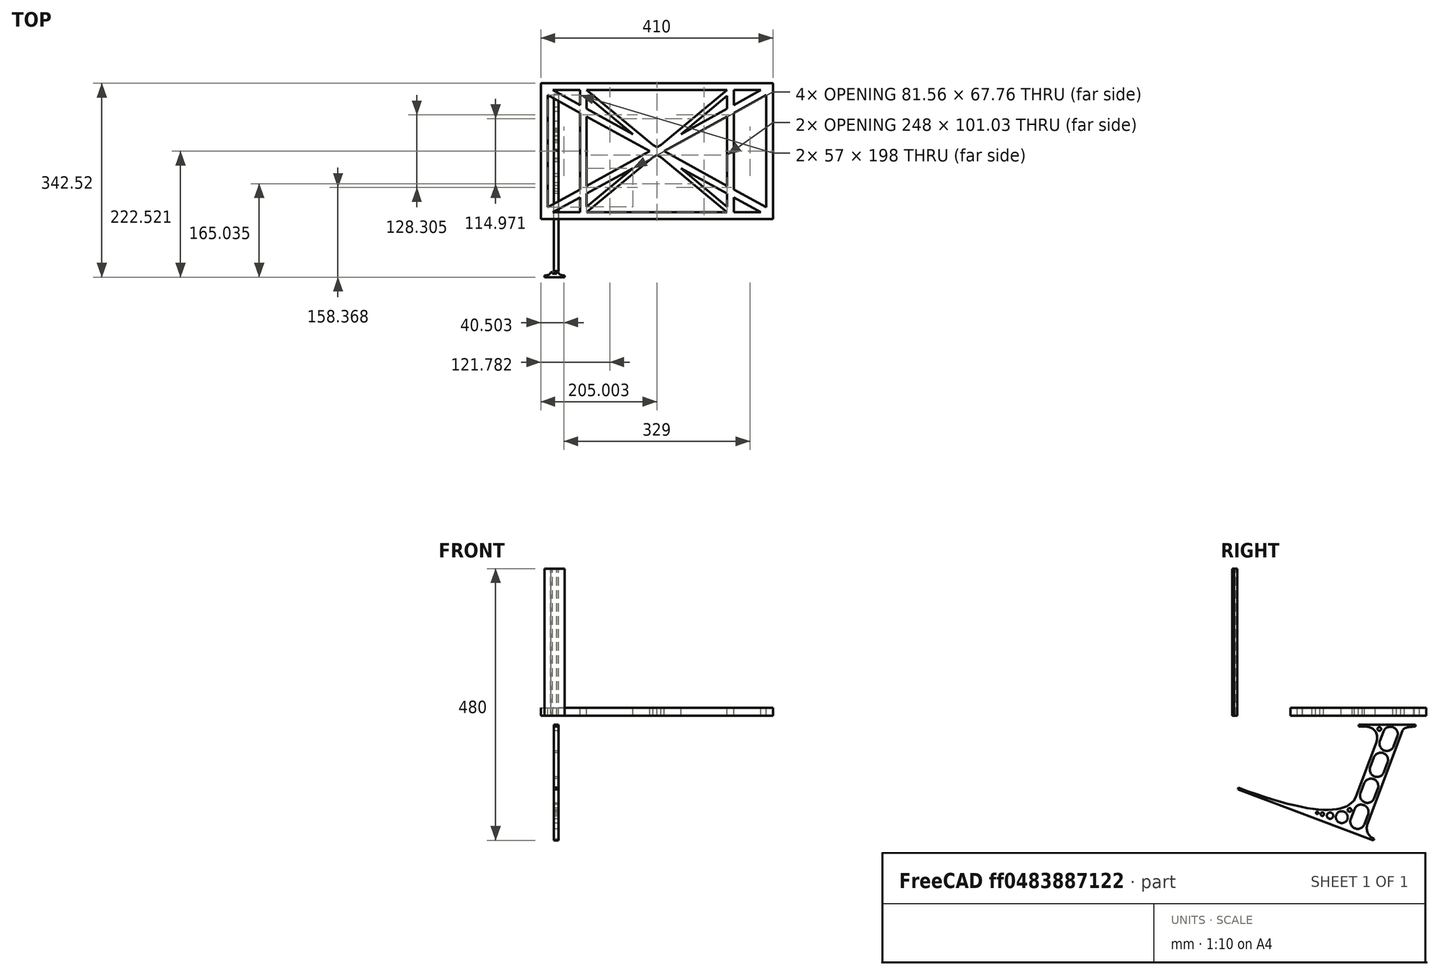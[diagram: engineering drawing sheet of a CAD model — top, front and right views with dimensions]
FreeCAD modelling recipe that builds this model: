
FCSTD DOCUMENT  (FreeCAD 0.19R0.19.2)
Label: laptopStand048
License: All rights reserved
LicenseURL: http://en.wikipedia.org/wiki/All_rights_reserved
objects: Sketcher::SketchObject×3, Part::Extrusion×3
note: 6 computed .brp shape members not serialized (recipe doc carries the construction recipe); baked Part::Feature solids carry a one-line shape summary decoded from their .brp

FEATURE [Sketcher::SketchObject] Sketch
  FullyConstrained = false
  sketch-geometry (70):
    g0: LineSegment StartX=-22.9272 StartY=136.221 StartZ=0 EndX=387.073 EndY=136.221 EndZ=0
    g1: LineSegment StartX=-22.9272 StartY=-103.779 StartZ=0 EndX=387.073 EndY=-103.779 EndZ=0
    g2: LineSegment StartX=375.073 StartY=115.221 StartZ=0 EndX=318.073 EndY=83.9235 EndZ=0
    g3: LineSegment StartX=-10.9272 StartY=-82.7794 StartZ=0 EndX=46.0728 EndY=-51.4823 EndZ=0
    g4: LineSegment StartX=-1.92719 StartY=124.221 StartZ=0 EndX=46.0728 EndY=97.8651 EndZ=0
    g5: LineSegment StartX=366.073 StartY=-91.7794 StartZ=0 EndX=318.073 EndY=-65.424 EndZ=0
    g6: LineSegment StartX=-10.9272 StartY=115.221 StartZ=0 EndX=-10.9272 EndY=-82.7794 EndZ=0
    g7: LineSegment StartX=375.073 StartY=-82.7794 StartZ=0 EndX=375.073 EndY=115.221 EndZ=0
    g8: LineSegment StartX=-1.92719 StartY=-91.7794 StartZ=0 EndX=46.0728 EndY=-91.7794 EndZ=0
    g9: LineSegment StartX=318.073 StartY=124.221 StartZ=0 EndX=366.073 EndY=124.221 EndZ=0
    g10: LineSegment StartX=306.073 StartY=-81.8102 StartZ=0 EndX=224.513 EndY=-14.0532 EndZ=0
    g11: LineSegment StartX=58.0728 StartY=114.251 StartZ=0 EndX=139.632 EndY=46.4944 EndZ=0
    g12: LineSegment StartX=306.073 StartY=124.221 StartZ=0 EndX=189.124 EndY=27.0628 EndZ=0
    g13: LineSegment StartX=58.0728 StartY=-91.7794 StartZ=0 EndX=175.022 EndY=5.37834 EndZ=0
    g14: LineSegment StartX=46.0728 StartY=124.221 StartZ=0 EndX=46.0728 EndY=97.8651 EndZ=0
    g15: LineSegment StartX=58.0728 StartY=-81.8102 StartZ=0 EndX=58.0728 EndY=-58.8351 EndZ=0
    g16: LineSegment StartX=318.073 StartY=124.221 StartZ=0 EndX=318.073 EndY=97.8651 EndZ=0
    g17: LineSegment StartX=306.073 StartY=114.251 StartZ=0 EndX=306.073 EndY=91.2763 EndZ=0
    g18: LineSegment StartX=224.513 StartY=46.4944 StartZ=0 EndX=306.073 EndY=114.251 EndZ=0
    g19: LineSegment StartX=175.022 StartY=27.0628 StartZ=0 EndX=58.0728 EndY=124.221 EndZ=0
    g20: LineSegment StartX=169.377 StartY=16.2206 StartZ=0 EndX=58.0728 EndY=77.3346 EndZ=0
    g21: LineSegment StartX=139.632 StartY=-14.0532 StartZ=0 EndX=58.0728 EndY=-81.8102 EndZ=0
    g22: LineSegment StartX=194.768 StartY=16.2206 StartZ=0 EndX=306.073 EndY=-44.8935 EndZ=0
    g23: LineSegment StartX=224.513 StartY=46.4944 StartZ=0 EndX=306.073 EndY=91.2763 EndZ=0
    g24: LineSegment StartX=175.022 StartY=27.0628 StartZ=0 EndX=179.022 EndY=24.8665 EndZ=0
    g25: LineSegment StartX=139.632 StartY=-14.0532 StartZ=0 EndX=58.0728 EndY=-58.8351 EndZ=0
    g26: LineSegment StartX=189.124 StartY=5.37834 StartZ=0 EndX=185.124 EndY=7.57463 EndZ=0
    g27: LineSegment StartX=189.124 StartY=5.37834 StartZ=0 EndX=306.073 EndY=-91.7794 EndZ=0
    g28: LineSegment StartX=306.073 StartY=77.3346 StartZ=0 EndX=306.073 EndY=-44.8935 EndZ=0
    g29: LineSegment StartX=318.073 StartY=83.9235 StartZ=0 EndX=318.073 EndY=-51.4823 EndZ=0
    g30: LineSegment StartX=318.073 StartY=97.8651 StartZ=0 EndX=366.073 EndY=124.221 EndZ=0
    g31: LineSegment StartX=306.073 StartY=77.3346 StartZ=0 EndX=194.768 EndY=16.2206 EndZ=0
    g32: LineSegment StartX=306.073 StartY=-58.8351 StartZ=0 EndX=224.513 EndY=-14.0532 EndZ=0
    g33: LineSegment StartX=306.073 StartY=-58.8351 StartZ=0 EndX=306.073 EndY=-81.8102 EndZ=0
    g34: LineSegment StartX=318.073 StartY=-51.4823 StartZ=0 EndX=375.073 EndY=-82.7794 EndZ=0
    g35: LineSegment StartX=318.073 StartY=-65.424 StartZ=0 EndX=318.073 EndY=-91.7794 EndZ=0
    g36: LineSegment StartX=318.073 StartY=-91.7794 StartZ=0 EndX=366.073 EndY=-91.7794 EndZ=0
    g37: LineSegment StartX=58.0728 StartY=-44.8935 StartZ=0 EndX=58.0728 EndY=77.3346 EndZ=0
    g38: LineSegment StartX=46.0728 StartY=-65.424 StartZ=0 EndX=-1.92719 EndY=-91.7794 EndZ=0
    g39: LineSegment StartX=46.0728 StartY=-65.424 StartZ=0 EndX=46.0728 EndY=-91.7794 EndZ=0
    g40: LineSegment StartX=58.0728 StartY=-44.8935 StartZ=0 EndX=169.377 EndY=16.2206 EndZ=0
    g41: LineSegment StartX=58.0728 StartY=91.2763 StartZ=0 EndX=58.0728 EndY=114.251 EndZ=0
    g42: LineSegment StartX=46.0728 StartY=83.9235 StartZ=0 EndX=46.0728 EndY=-51.4823 EndZ=0
    g43: LineSegment StartX=46.0728 StartY=124.221 StartZ=0 EndX=-1.92719 EndY=124.221 EndZ=0
    g44: LineSegment StartX=58.0728 StartY=91.2763 StartZ=0 EndX=139.632 EndY=46.4944 EndZ=0
    g45: LineSegment StartX=46.0728 StartY=83.9235 StartZ=0 EndX=-10.9272 EndY=115.221 EndZ=0
    g46: LineSegment StartX=-22.9272 StartY=136.221 StartZ=0 EndX=-42.9272 EndY=136.221 EndZ=0
    g47: LineSegment StartX=387.073 StartY=136.221 StartZ=0 EndX=407.073 EndY=136.221 EndZ=0
    g48: LineSegment StartX=-42.9272 StartY=136.221 StartZ=0 EndX=-42.9272 EndY=-103.779 EndZ=0
    g49: LineSegment StartX=-22.9272 StartY=-103.779 StartZ=0 EndX=-42.9272 EndY=-103.779 EndZ=0
    g50: LineSegment StartX=407.073 StartY=136.221 StartZ=0 EndX=407.073 EndY=-103.779 EndZ=0
    g51: LineSegment StartX=387.073 StartY=-103.779 StartZ=0 EndX=407.073 EndY=-103.779 EndZ=0
    g52: LineSegment StartX=179.022 StartY=27.0628 StartZ=0 EndX=179.022 EndY=124.221 EndZ=0
    g53: LineSegment StartX=185.124 StartY=27.0628 StartZ=0 EndX=185.124 EndY=124.221 EndZ=0
    g54: LineSegment StartX=179.022 StartY=27.0628 StartZ=0 EndX=179.022 EndY=24.8665 EndZ=0
    g55: LineSegment StartX=185.124 StartY=27.0628 StartZ=0 EndX=185.124 EndY=24.8665 EndZ=0
    g56: LineSegment StartX=185.124 StartY=7.57463 StartZ=0 EndX=185.124 EndY=-91.7794 EndZ=0
    g57: LineSegment StartX=179.022 StartY=7.57463 StartZ=0 EndX=179.022 EndY=-91.7794 EndZ=0
    g58: LineSegment StartX=189.124 StartY=27.0628 StartZ=0 EndX=185.124 EndY=24.8665 EndZ=0
    g59: LineSegment StartX=175.022 StartY=5.37834 StartZ=0 EndX=179.022 EndY=7.57463 EndZ=0
    g60: ArcOfCircle CenterX=-26.9272 CenterY=22.1087 CenterZ=0 NormalX=0 NormalY=0 NormalZ=1 AngleXU=0 Radius=8 StartAngle=1e-16 EndAngle=3.14159
    g61: ArcOfCircle CenterX=-26.9272 CenterY=-83.7794 CenterZ=0 NormalX=0 NormalY=0 NormalZ=1 AngleXU=0 Radius=8 StartAngle=3.14159 EndAngle=6.28319
    g62: LineSegment StartX=-34.9272 StartY=22.1087 StartZ=0 EndX=-34.9272 EndY=-83.7794 EndZ=0
    g63: LineSegment StartX=-18.9272 StartY=22.1087 StartZ=0 EndX=-18.9272 EndY=-83.7794 EndZ=0
    g64: LineSegment StartX=407.073 StartY=-91.7794 StartZ=0 EndX=391.073 EndY=-91.7794 EndZ=0
    g65: LineSegment StartX=391.073 StartY=-91.7794 StartZ=0 EndX=391.073 EndY=-83.7794 EndZ=0
    g66: LineSegment StartX=185.124 StartY=-91.7794 StartZ=0 EndX=306.073 EndY=-91.7794 EndZ=0
    g67: LineSegment StartX=179.022 StartY=-91.7794 StartZ=0 EndX=58.0728 EndY=-91.7794 EndZ=0
    g68: LineSegment StartX=306.073 StartY=124.221 StartZ=0 EndX=185.124 EndY=124.221 EndZ=0
    g69: LineSegment StartX=179.022 StartY=124.221 StartZ=0 EndX=58.0728 EndY=124.221 EndZ=0
  constraints (143):
    c: Horizontal(g0)
    c: Distance(g0) = 410
    c: Horizontal(g1)
    c: Block(g0)
    c: Horizontal(g8)
    c: Horizontal(g9)
    c: Tangent(g5,g20)
    c: PointOnObject(g20,g3)
    c: PointOnObject(g22,g2)
    c: Coincident(g44,g11)
    c: Coincident(g24,g19)
    c: Coincident(g18,g23)
    c: Coincident(g25,g21)
    c: Coincident(g32,g10)
    c: Coincident(g27,g26)
    c: Coincident(g18,g17)
    c: Tangent(g17,g28)
    c: Tangent(g16,g29)
    c: Coincident(g23,g17)
    c: Tangent(g23,g30)
    c: Coincident(g2,g29)
    c: Coincident(g31,g28)
    c: Tangent(g2,g31)
    c: Coincident(g33,g10)
    c: Tangent(g5,g32)
    c: Tangent(g28,g33)
    c: Coincident(g22,g28)
    c: Tangent(g22,g34)
    c: Coincident(g29,g34)
    c: Coincident(g35,g5)
    c: Tangent(g29,g35)
    c: Coincident(g21,g15)
    c: Tangent(g15,g37)
    c: Coincident(g25,g15)
    c: Tangent(g25,g38)
    c: Coincident(g39,g38)
    c: Tangent(g14,g39)
    c: Coincident(g3,g42)
    c: Coincident(g40,g37)
    c: Tangent(g3,g40)
    c: Tangent(g37,g41)
    c: Tangent(g14,g42)
    c: Coincident(g11,g41)
    c: Coincident(g4,g14)
    c: Coincident(g44,g41)
    c: Tangent(g4,g44)
    c: Coincident(g20,g37)
    c: Coincident(g45,g42)
    c: Tangent(g20,g45)
    c: Block(g19)
    c: Block(g12)
    c: Block(g16)
    c: Block(g30)
    c: Block(g2)
    c: Block(g34)
    c: Block(g7)
    c: Block(g32)
    c: Block(g33)
    c: Block(g5)
    c: Block(g35)
    c: Block(g18)
    c: Block(g27)
    c: Block(g13)
    c: Block(g25)
    c: Block(g21)
    c: Block(g39)
    c: Block(g38)
    c: Block(g3)
    c: Block(g6)
    c: Block(g45)
    c: Block(g4)
    c: Block(g14)
    c: Block(g11)
    c: Block(g41)
    c: Block(g31)
    c: Block(g28)
    c: Block(g20)
    c: Block(g40)
    c: Block(g43)
    c: Block(g9)
    c: Block(g36)
    c: Block(g8)
    c: Horizontal(g46)
    c: Distance(g46) = 20
    c: Coincident(g47,g0)
    c: Horizontal(g47)
    c: Distance(g47) = 20
    c: Coincident(g48,g46)
    c: Vertical(g48)
    c: Horizontal(g49)
    c: Coincident(g49,g48)
    c: Coincident(g50,g47)
    c: Vertical(g50)
    c: Coincident(g51,g1)
    c: Horizontal(g51)
    c: Coincident(g51,g50)
    c: Block(g50)
    c: Block(g49)
    c: Block(g48)
    c: Block(g1)
    c: Vertical(g52)
    c: Vertical(g53)
    c: Vertical(g54)
    c: Vertical(g55)
    c: Tangent(g55,g56)
    c: Tangent(g54,g57)
    c: Coincident(g24,g54)
    c: Coincident(g26,g56)
    c: Block(g52)
    c: Block(g53)
    c: Block(g57)
    c: Block(g56)
    c: Coincident(g58,g12)
    c: Coincident(g58,g55)
    c: Coincident(g59,g13)
    c: Coincident(g59,g57)
    c: Tangent(g60,g63) = 1.5708
    c: Tangent(g60,g62) = -1.5708
    c: Tangent(g62,g61) = -1.5708
    c: Tangent(g63,g61) = 1.5708
    c: Vertical(g62)
    c: Equal(g60,g61)
    c: Block(g63)
    c: Block(g62)
    c: PointOnObject(g64,g50)
    c: Horizontal(g64)
    c: Distance(g64) = 16
    c: Block(g64)
    c: Coincident(g65,g64)
    c: Vertical(g65)
    c: Distance(g65) = 8
    c: Coincident(g66,g56)
    c: Coincident(g66,g27)
    c: Horizontal(g66)
    c: Coincident(g67,g57)
    c: Coincident(g67,g13)
    c: Horizontal(g67)
    c: Coincident(g68,g12)
    c: Coincident(g68,g53)
    c: Horizontal(g68)
    c: Coincident(g69,g52)
    c: Coincident(g69,g19)
    c: Horizontal(g69)
FEATURE [Sketcher::SketchObject] Sketch001
  FullyConstrained = true
  MapMode = 4
  Placement = pos=(0,0,0) rot=(0.57735,0.57735,0.57735;2.0944rad)
  Support = -> [Sketch]
  sketch-geometry (46):
    g0: BSplineCurve PolesCount=3 KnotsCount=2 Degree=2 IsPeriodic=0
    g1: ArcOfCircle CenterX=73.122 CenterY=-32.2909 CenterZ=0 NormalX=0 NormalY=0 NormalZ=1 AngleXU=0 Radius=13 StartAngle=5.92268 EndAngle=9.06428
    g2: ArcOfCircle CenterX=66.7816 CenterY=-49.1439 CenterZ=0 NormalX=0 NormalY=0 NormalZ=1 AngleXU=0 Radius=13 StartAngle=2.78068 EndAngle=5.92131
    g3: ArcOfCircle CenterX=55.9263 CenterY=-78.1807 CenterZ=0 NormalX=0 NormalY=0 NormalZ=1 AngleXU=0 Radius=13 StartAngle=5.92268 EndAngle=9.06428
    g4: ArcOfCircle CenterX=49.5884 CenterY=-95.0342 CenterZ=0 NormalX=0 NormalY=0 NormalZ=1 AngleXU=0 Radius=13 StartAngle=2.78068 EndAngle=5.92131
    g5: ArcOfCircle CenterX=38.7206 CenterY=-124.067 CenterZ=0 NormalX=0 NormalY=0 NormalZ=1 AngleXU=0 Radius=13 StartAngle=5.92268 EndAngle=9.06428
    g6: ArcOfCircle CenterX=32.3875 CenterY=-140.92 CenterZ=0 NormalX=0 NormalY=0 NormalZ=1 AngleXU=0 Radius=13 StartAngle=2.78068 EndAngle=5.92131
    g7: ArcOfCircle CenterX=21.4715 CenterY=-169.934 CenterZ=0 NormalX=0 NormalY=0 NormalZ=1 AngleXU=0 Radius=13 StartAngle=5.92268 EndAngle=9.06428
    g8: ArcOfCircle CenterX=15.1336 CenterY=-186.787 CenterZ=0 NormalX=0 NormalY=0 NormalZ=1 AngleXU=0 Radius=13 StartAngle=2.78068 EndAngle=5.92131
    g9-g12: Circle x4 (B-spline internal-alignment scaffolding for g13; pole/knot coordinates omitted)
    g13: BSplineCurve PolesCount=4 KnotsCount=2 Degree=3 IsPeriodic=0
    g14: GeomPoint X=28.8094 Y=-19.0875 Z=0
    g15: GeomPoint X=47.0443 Y=-50.4712 Z=0
    g16: Circle CenterX=53.5586 CenterY=-23.2695 CenterZ=0 NormalX=0 NormalY=0 NormalZ=1 AngleXU=0 Radius=3.24518
    g17: Circle CenterX=-195.441 CenterY=-127.082 CenterZ=0 NormalX=0 NormalY=0 NormalZ=1 AngleXU=0 Radius=1
    g18: Circle CenterX=-8.24091 CenterY=-197.481 CenterZ=0 NormalX=0 NormalY=0 NormalZ=1 AngleXU=0 Radius=1
    g19: Circle CenterX=12.8789 CenterY=-141.321 CenterZ=0 NormalX=0 NormalY=0 NormalZ=1 AngleXU=0 Radius=1
    g20: BSplineCurve PolesCount=3 KnotsCount=2 Degree=2 IsPeriodic=0
    g21: GeomPoint X=-195.441 Y=-127.082 Z=0
    g22: GeomPoint X=12.8789 Y=-141.321 Z=0
    g23: Circle CenterX=-12.8016 CenterY=-179.036 CenterZ=0 NormalX=0 NormalY=0 NormalZ=1 AngleXU=0 Radius=10.5072
    g24: Circle CenterX=0.933922 CenterY=-166.43 CenterZ=0 NormalX=0 NormalY=0 NormalZ=1 AngleXU=0 Radius=3.26661
    g25: Circle CenterX=-33.5518 CenterY=-176.44 CenterZ=0 NormalX=0 NormalY=0 NormalZ=1 AngleXU=0 Radius=5.64388
    g26: Circle CenterX=-47.2366 CenterY=-173.859 CenterZ=0 NormalX=0 NormalY=0 NormalZ=1 AngleXU=0 Radius=3.01653
    g27: Circle CenterX=-56.2595 CenterY=-171.456 CenterZ=0 NormalX=0 NormalY=0 NormalZ=1 AngleXU=0 Radius=2.12826
    g28: ArcOfCircle CenterX=51.2151 CenterY=-198.473 CenterZ=0 NormalX=0 NormalY=0 NormalZ=1 AngleXU=0 Radius=20 StartAngle=2.78189 EndAngle=4.35269
    g29: LineSegment StartX=32.4951 StartY=-191.433 StartZ=0 EndX=94.6577 EndY=-26.1351 EndZ=0
    g30: LineSegment StartX=43.1192 StartY=-220.001 StartZ=0 EndX=-196.497 EndY=-129.89 EndZ=0
    g31: LineSegment StartX=43.1192 StartY=-220.001 StartZ=0 EndX=44.1752 EndY=-217.193 EndZ=0
    g32: LineSegment StartX=117.223 StartY=-19.0875 StartZ=0 EndX=117.223 EndY=-16.0875 EndZ=0
    g33: LineSegment StartX=117.223 StartY=-16.0875 StartZ=0 EndX=17.2232 EndY=-16.0875 EndZ=0
    g34: LineSegment StartX=17.2232 StartY=-16.0875 StartZ=0 EndX=17.2232 EndY=-19.0875 EndZ=0
    g35: LineSegment StartX=28.8094 StartY=-19.0875 StartZ=0 EndX=17.2232 EndY=-19.0875 EndZ=0
    g36: LineSegment StartX=47.0443 StartY=-50.4712 StartZ=0 EndX=12.8789 EndY=-141.321 EndZ=0
    g37: LineSegment StartX=-195.441 StartY=-127.082 StartZ=0 EndX=-196.497 EndY=-129.89 EndZ=0
    g38: LineSegment StartX=85.2864 StartY=-36.8765 StartZ=0 EndX=78.9396 EndY=-53.7463 EndZ=0
    g39: LineSegment StartX=60.9577 StartY=-27.7052 StartZ=0 EndX=54.6191 EndY=-44.5532 EndZ=0
    g40: LineSegment StartX=68.0907 StartY=-82.7664 StartZ=0 EndX=61.7465 EndY=-99.6365 EndZ=0
    g41: LineSegment StartX=43.7619 StartY=-73.595 StartZ=0 EndX=37.426 EndY=-90.4435 EndZ=0
    g42: LineSegment StartX=50.885 StartY=-128.652 StartZ=0 EndX=44.5456 EndY=-145.522 EndZ=0
    g43: LineSegment StartX=26.5562 StartY=-119.481 StartZ=0 EndX=20.2251 EndY=-136.329 EndZ=0
    g44: LineSegment StartX=9.3071 StartY=-165.349 StartZ=0 EndX=2.97115 EndY=-182.197 EndZ=0
    g45: LineSegment StartX=33.6358 StartY=-174.52 StartZ=0 EndX=27.2917 EndY=-191.39 EndZ=0
  constraints (70):
    c: Block(g0)
    c: Block(g1)
    c: Block(g2)
    c: Block(g4)
    c: Block(g3)
    c: Block(g6)
    c: Block(g5)
    c: Block(g8)
    c: Block(g7)
    c: Weight(g9) = 1
    c: Equal(g9,g10)
    c: Equal(g9,g11)
    c: Equal(g9,g12)
    c: InternalAlignment(g9-g12 -> g13) x4
    c: InternalAlignment(g14,g13)
    c: InternalAlignment(g15,g13)
    c: Block(g16)
    c: Weight(g17) = 1
    c: Equal(g17,g18)
    c: Equal(g17,g19)
    c: InternalAlignment(g17,g20)
    c: InternalAlignment(g18,g20)
    c: InternalAlignment(g19,g20)
    c: InternalAlignment(g21,g20)
    c: InternalAlignment(g22,g20)
    c: Block(g20)
    c: Block(g23)
    c: Block(g24)
    c: Block(g25)
    c: Block(g26)
    c: Block(g27)
    c: Block(g28)
    c: Coincident(g29,g28)
    c: Coincident(g29,g0)
    c: Block(g13)
    c: Coincident(g31,g30)
    c: Coincident(g31,g28)
    c: Block(g31)
    c: Coincident(g32,g0)
    c: Vertical(g32)
    c: Coincident(g33,g32)
    c: Horizontal(g33)
    c: Coincident(g34,g33)
    c: Vertical(g34)
    c: Block(g33)
    c: Coincident(g35,g13)
    c: Coincident(g35,g34)
    c: Horizontal(g35)
    c: Coincident(g36,g13)
    c: Coincident(g36,g20)
    c: Coincident(g37,g20)
    c: Coincident(g37,g30)
    c: Block(g30)
    c: Coincident(g38,g1)
    c: Coincident(g38,g2)
    c: Coincident(g39,g1)
    c: Coincident(g39,g2)
    c: Coincident(g40,g3)
    c: Coincident(g40,g4)
    c: Coincident(g41,g3)
    c: Coincident(g41,g4)
    c: Coincident(g42,g5)
    c: Coincident(g42,g6)
    c: Coincident(g43,g5)
    c: Coincident(g43,g6)
    c: Coincident(g44,g7)
    c: Coincident(g44,g8)
    c: Coincident(g45,g7)
    c: Coincident(g45,g8)
    c: Distance(g30) = 256
FEATURE [Part::Extrusion] Extrude002
  Base = -> Sketch001
  Dir = (1,0,0)
  DirMode = 2
  FaceMakerClass = Part::FaceMakerBullseye
  LengthFwd = 8
  LengthRev = 0
  Solid = true
  Symmetric = false
FEATURE [Sketcher::SketchObject] Sketch002
  FullyConstrained = true
  sketch-geometry (20):
    g0: LineSegment StartX=-2.77179 StartY=-200.304 StartZ=0 EndX=5.22821 EndY=-200.304 EndZ=0
    g1: LineSegment StartX=5.22821 StartY=-200.304 StartZ=0 EndX=5.22821 EndY=-197.304 EndZ=0
    g2: LineSegment StartX=-2.77179 StartY=-200.304 StartZ=0 EndX=-2.77179 EndY=-197.304 EndZ=0
    g3: LineSegment StartX=5.22821 StartY=-197.304 StartZ=0 EndX=8.22821 EndY=-197.304 EndZ=0
    g4: LineSegment StartX=-2.77179 StartY=-197.304 StartZ=0 EndX=-5.77179 EndY=-197.304 EndZ=0
    g5: LineSegment StartX=19.2282 StartY=-203.304 StartZ=0 EndX=19.2282 EndY=-206.304 EndZ=0
    g6: LineSegment StartX=-16.7718 StartY=-203.304 StartZ=0 EndX=-16.7718 EndY=-206.304 EndZ=0
    g7: LineSegment StartX=-16.7718 StartY=-206.304 StartZ=0 EndX=19.2282 EndY=-206.304 EndZ=0
    g8: Circle CenterX=-16.7718 CenterY=-203.304 CenterZ=0 NormalX=0 NormalY=0 NormalZ=1 AngleXU=0 Radius=1
    g9: Circle CenterX=-5.77179 CenterY=-203.304 CenterZ=0 NormalX=0 NormalY=0 NormalZ=1 AngleXU=0 Radius=1
    g10: Circle CenterX=-5.77179 CenterY=-197.304 CenterZ=0 NormalX=0 NormalY=0 NormalZ=1 AngleXU=0 Radius=1
    g11: BSplineCurve PolesCount=3 KnotsCount=2 Degree=2 IsPeriodic=0
    g12: GeomPoint X=-16.7718 Y=-203.304 Z=0
    g13: GeomPoint X=-5.77179 Y=-197.304 Z=0
    g14: Circle CenterX=19.2282 CenterY=-203.304 CenterZ=0 NormalX=0 NormalY=0 NormalZ=1 AngleXU=0 Radius=1
    g15: Circle CenterX=8.22821 CenterY=-203.304 CenterZ=0 NormalX=0 NormalY=0 NormalZ=1 AngleXU=0 Radius=1
    g16: Circle CenterX=8.22821 CenterY=-197.304 CenterZ=0 NormalX=0 NormalY=0 NormalZ=1 AngleXU=0 Radius=1
    g17: BSplineCurve PolesCount=3 KnotsCount=2 Degree=2 IsPeriodic=0
    g18: GeomPoint X=19.2282 Y=-203.304 Z=0
    g19: GeomPoint X=8.22821 Y=-197.304 Z=0
  constraints (41):
    c: Horizontal(g0)
    c: Distance(g0) = 8
    c: Coincident(g1,g0)
    c: Vertical(g1)
    c: Distance(g1) = 3
    c: Coincident(g2,g0)
    c: Vertical(g2)
    c: Distance(g2) = 3
    c: Coincident(g3,g1)
    c: Horizontal(g3)
    c: Distance(g3) = 3
    c: Coincident(g4,g2)
    c: Horizontal(g4)
    c: Distance(g4) = 3
    c: Vertical(g5)
    c: Vertical(g6)
    c: Coincident(g7,g6)
    c: Coincident(g7,g5)
    c: Weight(g8) = 1
    c: Equal(g8,g9)
    c: Equal(g8,g10)
    c: Coincident(g11,g4)
    c: InternalAlignment(g8,g11)
    c: InternalAlignment(g9,g11)
    c: InternalAlignment(g10,g11)
    c: InternalAlignment(g12,g11)
    c: InternalAlignment(g13,g11)
    c: Coincident(g17,g5)
    c: Weight(g14) = 1
    c: Equal(g14,g15)
    c: Equal(g14,g16)
    c: Coincident(g17,g3)
    c: InternalAlignment(g14,g17)
    c: InternalAlignment(g15,g17)
    c: InternalAlignment(g16,g17)
    c: InternalAlignment(g18,g17)
    c: InternalAlignment(g19,g17)
    c: Block(g7)
    c: Block(g17)
    c: Block(g11)
    c: Block(g6)
FEATURE [Part::Extrusion] Extrude003
  Base = -> Sketch002
  Dir = (0,0,1)
  DirMode = 2
  FaceMakerClass = Part::FaceMakerBullseye
  LengthFwd = 260
  LengthRev = 0
  Solid = true
  Symmetric = false
FEATURE [Part::Extrusion] Extrude
  Base = -> Sketch
  Dir = (0,0,1)
  DirMode = 2
  FaceMakerClass = Part::FaceMakerBullseye
  LengthFwd = 14
  LengthRev = 0
  Solid = true
  Symmetric = false
